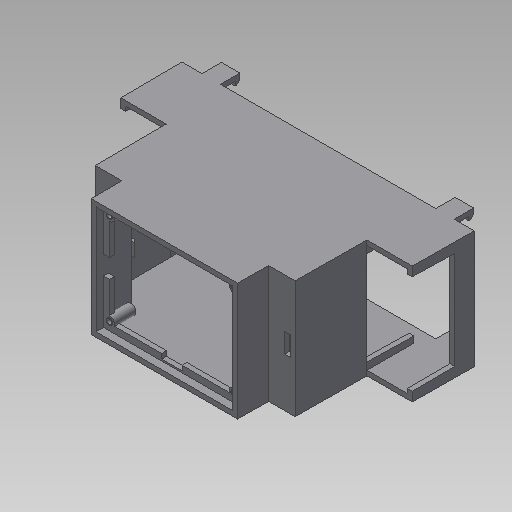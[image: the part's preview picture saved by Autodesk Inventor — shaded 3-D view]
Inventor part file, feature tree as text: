
AUTODESK INVENTOR PART (.ipt)
format: ipt  version: 2018 (Build 220112000, 112)  size: 463,360 bytes
history: native  units: mm
features: sketch x12, extrude x11, other x6, mirror x4, projected_geometry x3, hole x1, revolve x1, fillet x1
ambient origin geometry x8: Origin, YZ Plane, XZ Plane, XY Plane, X Axis, Y Axis, Z Axis, Center Point
bodies: Body1 (feature_tree)
feature tree (39):
  other  "Твердое тело1"
  extrude  "Выдавливание1"  Depth=1.5mm
  extrude  "Выдавливание2"  Depth=1.5mm
  extrude  "Выдавливание3"  Depth=1.5mm
  other  "РабПлоскость6"
  extrude  "Выдавливание4"  Depth=1.5mm
  extrude  "Выдавливание5"  Depth=1.5mm
  extrude  "Выдавливание6"  Depth=1.5mm
  hole  "Отверстие2"  [1 undecoded]
  extrude  "Выдавливание7"  Depth=1.5mm
  extrude  "Выдавливание8"  Depth=1.5mm
  other  "РабПлоскость8"
  revolve  "Вращение1"
  mirror  "Зеркальное отражение1"
  mirror  "Зеркальное отражение2"
  extrude  "Выдавливание9"  Depth=1.5mm
  other  "РабПлоскость10"
  extrude  "Выдавливание10"  Depth=90.2mm
  mirror  "Зеркальное отражение3"
  other  "РабПлоскость11"
  extrude  "Выдавливание11"  Depth=89.9mm
  mirror  "Зеркальное отражение4"
  fillet  "Сопряжение1"  Radius=19.0mm
  sketch  "Эскиз10"
  sketch  "Эскиз11"
  projected_geometry  "Спроецированная петля1"
  sketch  "Эскиз12"
  projected_geometry  "Спроецированная петля2"
  sketch  "Эскиз13"
  sketch  "Эскиз14"
  sketch  "Эскиз15"
  projected_geometry  "Спроецированная петля3"
  sketch  "Эскиз16"
  sketch  "Эскиз17"
  sketch  "Эскиз18"
  sketch  "Эскиз19"
  other  "РабПлоскость9"
  sketch  "Эскиз20"
  sketch  "Эскиз21"
note: 1 required parameter value undecoded (feature->parameter linkage not recoverable at this tier; creation-order binding heuristic only, values carry confidence <= 0.55)
